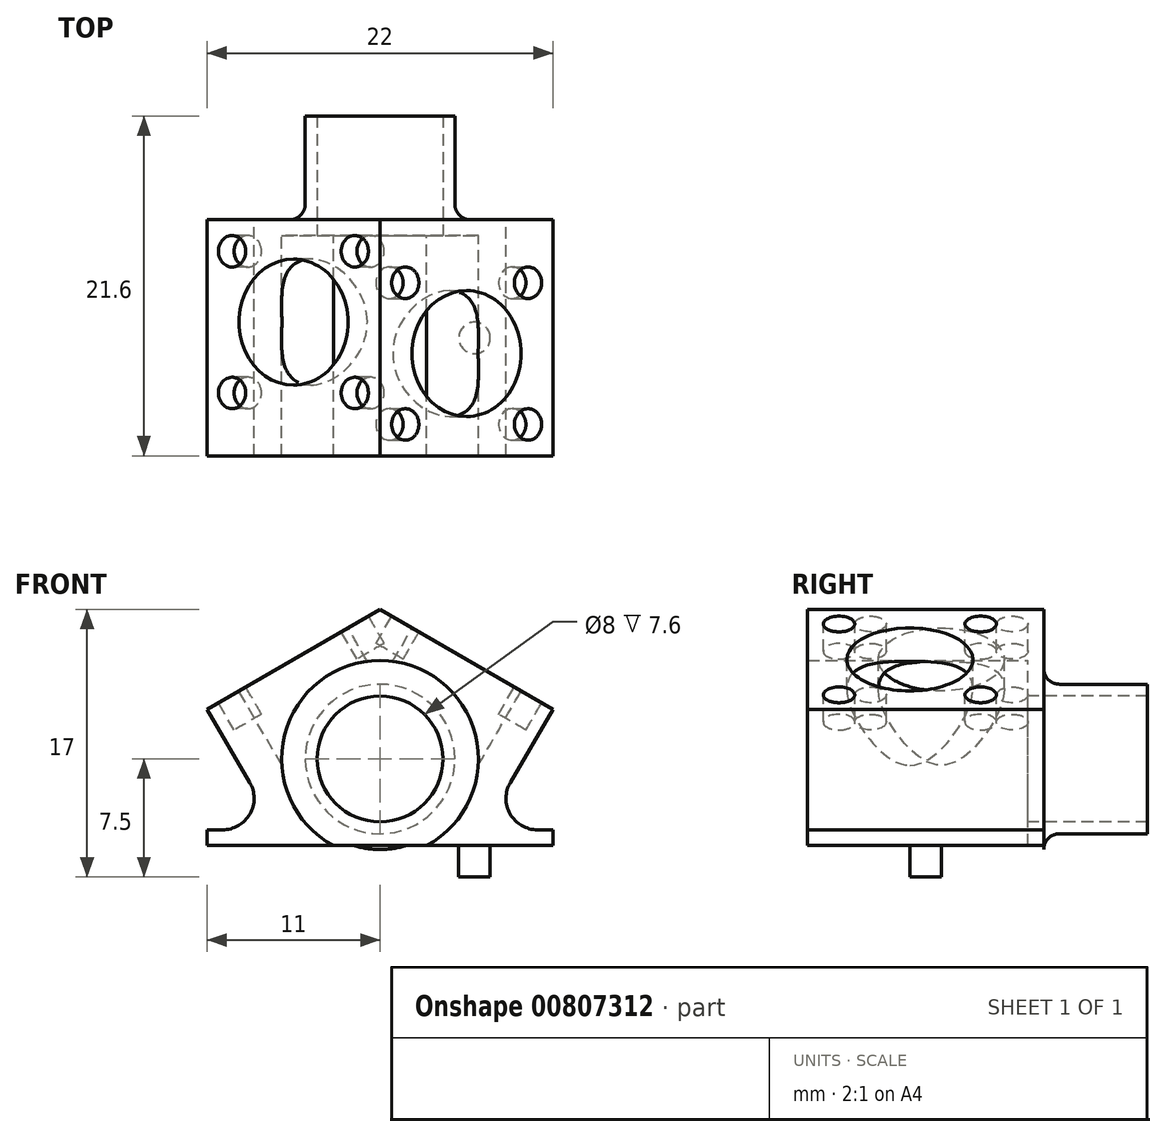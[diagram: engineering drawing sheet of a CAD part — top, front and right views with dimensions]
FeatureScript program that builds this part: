
annotation { "Feature Type Name" : "Feature", "Feature Type Description" : "" }
export const myFeature = defineFeature(function(context is Context, id is Id, definition is map)
    precondition{}
    {
        {
            var Q0;
            Q0=qCreatedBy(makeId("Front.planeOp"),FACE);
            var sketch = newSketch(context, id + "F0", { "sketchPlane" : qUnion([Q0])});
            skCircle(sketch, "E0", {"center": v(0, 0) * mm, "radius": 4 * mm});
            skCircle(sketch, "E1", {"center": v(0, 0) * mm, "radius": 6.25 * mm});
            skLineSegment(sketch, "E2", {"start": v(0, 9.5) * mm, "end": v(0, -7.5) * mm, "construction": true});
            skLineSegment(sketch, "E3", {"start": v(-11, 0) * mm, "end": v(11, 0) * mm, "construction": true});
            skLineSegment(sketch, "E4", {"start": v(-11, -7.5) * mm, "end": v(11, -7.5) * mm});
            skPoint(sketch, "E5", {"position": v(0, -7.5) * mm});
            skLineSegment(sketch, "E6", {"start": v(-11, -7.5) * mm, "end": v(-11, 9.5) * mm});
            skLineSegment(sketch, "E7.MirrorCS", {"start": v(11, -7.5) * mm, "end": v(11, 9.5) * mm});
            skLineSegment(sketch, "E8", {"start": v(-11, 9.5) * mm, "end": v(11, 9.5) * mm});
            skLineSegment(sketch, "E9", {"start": v(0, 9.5) * mm, "end": v(-11, 3.15) * mm});
            skLineSegment(sketch, "E10.MirrorCS", {"start": v(0, 9.5) * mm, "end": v(11, 3.15) * mm});
            skPoint(sketch, "E11", {"position": v(-11, -4.5) * mm});
            skArc(sketch, "E12", {"start": v(-11, -0.77) * mm, "mid": v(-12, -2.5) * mm, "end": v(-11, -4.23) * mm, "construction": true});
            skArc(sketch, "E13", {"start": v(-11, -4.23) * mm, "mid": v(-10.52, -4.43) * mm, "end": v(-10, -4.5) * mm, "construction": true});
            skLineSegment(sketch, "E14", {"start": v(-11, 3.15) * mm, "end": v(-8.28, -1.49) * mm});
            skArc(sketch, "E15", {"start": v(-8.28, -1.49) * mm, "mid": v(-9.49, -0.57) * mm, "end": v(-11, -0.77) * mm, "construction": true});
            skLineSegment(sketch, "E16", {"start": v(-11, -4.5) * mm, "end": v(-10, -4.5) * mm});
            skArc(sketch, "E17", {"start": v(-10, -4.5) * mm, "mid": v(-8.26, -3.5) * mm, "end": v(-8.28, -1.49) * mm});
            skLineSegment(sketch, "E18.MirrorCS", {"start": v(11, 3.15) * mm, "end": v(8.28, -1.49) * mm});
            skArc(sketch, "E19.MirrorCS", {"start": v(10, -4.5) * mm, "mid": v(8.26, -3.5) * mm, "end": v(8.28, -1.49) * mm});
            skLineSegment(sketch, "E20.MirrorCS", {"start": v(11, -4.5) * mm, "end": v(10, -4.5) * mm});
            skCircle(sketch, "E21", {"center": v(0, 0) * mm, "radius": 4.75 * mm});
            skSolve(sketch);
        }
        {
            var Q0;
            Q0=makeQuery(id+"F0.imprint","IMPRINT",FACE,{"disambiguationData":[TD([[makeQuery(id+"F0.imprint","IMPRINT",EDGE,{"derivedFrom":sQuery(id+"F0.wireOp",EDGE,"E1")}),-1.0]])]});
            extrude(context, id + "F1", {"entities" : qUnion([Q0]), "depth" : 13 * mm, "offsetDistance" : 25 * mm});
        }
        {
            var Q0;
            Q0=makeQuery(id+"F0.imprint","IMPRINT",FACE,{"disambiguationData":[TD([[makeQuery(id+"F0.imprint","IMPRINT",EDGE,{"derivedFrom":sQuery(id+"F0.wireOp",EDGE,"E1")}),1.0]])]});
            var Q1;
            Q1=makeQuery(id+"F0.imprint","IMPRINT",FACE,{"disambiguationData":[TD([[makeQuery(id+"F0.imprint","IMPRINT",EDGE,{"derivedFrom":sQuery(id+"F0.wireOp",EDGE,"E0")}),-1.0]])]});
            var Q2;
            Q2=makeQuery(id+"F0.imprint","IMPRINT",FACE,{"disambiguationData":[TD([[makeQuery(id+"F0.imprint","IMPRINT",EDGE,{"derivedFrom":sQuery(id+"F0.wireOp",EDGE,"E1")}),-1.0]])]});
            extrude(context, id + "F2", {"entities" : qUnion([Q0, Q1, Q2]), "operationType" : NewBodyOperationType.ADD, "oppositeDirection" : true, "depth" : 2 * mm, "offsetDistance" : 25 * mm});
        }
        {
            var Q0;
            Q0=makeQuery(id+"F0.imprint","IMPRINT",FACE,{"disambiguationData":[TD([[makeQuery(id+"F0.imprint","IMPRINT",EDGE,{"derivedFrom":sQuery(id+"F0.wireOp",EDGE,"E0")}),-1.0]])]});
            extrude(context, id + "F3", {"entities" : qUnion([Q0]), "operationType" : NewBodyOperationType.ADD, "oppositeDirection" : true, "depth" : 8.6 * mm, "offsetDistance" : 25 * mm});
        }
        {
            var Q0;
            Q0=makeQuery(id+"F3.boolean.opBoolean","INTERSECT",EDGE,{"derivedFrom":[makeQuery(id+"F2.opExtrude","CAP_FACE",FACE,{"disambiguationData":[OSD([sQuery(id+"F0.wireOp",EDGE,"E0"),sQuery(id+"F0.wireOp",EDGE,"E4"),sQuery(id+"F0.wireOp",EDGE,"E6"),sQuery(id+"F0.wireOp",EDGE,"E7.MirrorCS"),sQuery(id+"F0.wireOp",EDGE,"E9"),sQuery(id+"F0.wireOp",EDGE,"E10.MirrorCS"),sQuery(id+"F0.wireOp",EDGE,"E14"),sQuery(id+"F0.wireOp",EDGE,"E16"),sQuery(id+"F0.wireOp",EDGE,"E17"),sQuery(id+"F0.wireOp",EDGE,"E18.MirrorCS"),sQuery(id+"F0.wireOp",EDGE,"E19.MirrorCS"),sQuery(id+"F0.wireOp",EDGE,"E20.MirrorCS")])],"isStart":false}),makeQuery(id+"F3.opExtrude","SWEPT_FACE",FACE,{"disambiguationData":[OSD([sQuery(id+"F0.wireOp",EDGE,"E21")])]})]});
            fillet(context, id + "F4", {"entities" : qUnion([Q0]), "radius" : 1 * mm, "tangentPropagation" : true, "allowEdgeOverflow" : false});
        }
        {
            var Q0;
            {var subQ0=sQuery(id+"F0.wireOp",EDGE,"E10.MirrorCS");Q0=makeQuery(id+"F2.boolean.opBoolean","MERGE",FACE,{"derivedFrom":[makeQuery(id+"F1.opExtrude","SWEPT_FACE",FACE,{"disambiguationData":[OSD([subQ0])]}),makeQuery(id+"F2.opExtrude","SWEPT_FACE",FACE,{"disambiguationData":[OSD([subQ0])]})]});}
            var sketch = newSketch(context, id + "F5", { "sketchPlane" : qUnion([Q0])});
            skLineSegment(sketch, "E22.0", {"start": v(-4.75, -13) * mm, "end": v(7.95, -13) * mm});
            skLineSegment(sketch, "E23.0", {"start": v(-4.75, -13) * mm, "end": v(-4.75, 2) * mm});
            skLineSegment(sketch, "E24.0", {"start": v(-4.75, 2) * mm, "end": v(7.95, 2) * mm});
            skLineSegment(sketch, "E25.0", {"start": v(7.95, -13) * mm, "end": v(7.95, 2) * mm});
            skCircle(sketch, "E26", {"center": v(1.6, -6.5) * mm, "radius": 4 * mm});
            skLineSegment(sketch, "E27.bottom", {"start": v(-2.9, -2) * mm, "end": v(6.1, -2) * mm, "construction": true});
            skLineSegment(sketch, "E27.top", {"start": v(-2.9, -11) * mm, "end": v(6.1, -11) * mm, "construction": true});
            skLineSegment(sketch, "E27.left", {"start": v(-2.9, -2) * mm, "end": v(-2.9, -11) * mm, "construction": true});
            skLineSegment(sketch, "E27.right", {"start": v(6.1, -2) * mm, "end": v(6.1, -11) * mm, "construction": true});
            skCircle(sketch, "E28", {"center": v(-2.9, -11) * mm, "radius": 1 * mm});
            skCircle(sketch, "E29", {"center": v(6.1, -11) * mm, "radius": 1 * mm});
            skCircle(sketch, "E30", {"center": v(6.1, -2) * mm, "radius": 1 * mm});
            skCircle(sketch, "E31", {"center": v(-2.9, -2) * mm, "radius": 1 * mm});
            skSolve(sketch);
        }
        {
            var Q0;
            {var subQ0=sQuery(id+"F0.wireOp",EDGE,"E9");Q0=makeQuery(id+"F2.boolean.opBoolean","MERGE",FACE,{"derivedFrom":[makeQuery(id+"F1.opExtrude","SWEPT_FACE",FACE,{"disambiguationData":[OSD([subQ0])]}),makeQuery(id+"F2.opExtrude","SWEPT_FACE",FACE,{"disambiguationData":[OSD([subQ0])]})]});}
            var sketch = newSketch(context, id + "F6", { "sketchPlane" : qUnion([Q0])});
            skLineSegment(sketch, "E32.0", {"start": v(4.75, 2) * mm, "end": v(-7.95, 2) * mm});
            skLineSegment(sketch, "E33.0", {"start": v(4.75, -13) * mm, "end": v(4.75, 2) * mm});
            skLineSegment(sketch, "E34.0", {"start": v(4.75, -13) * mm, "end": v(-7.95, -13) * mm});
            skLineSegment(sketch, "E35.0", {"start": v(-7.95, -13) * mm, "end": v(-7.95, 2) * mm});
            skCircle(sketch, "E36", {"center": v(-1.6, -4.5) * mm, "radius": 4 * mm});
            skLineSegment(sketch, "E37.bottom", {"start": v(-6.1, 0) * mm, "end": v(2.9, 0) * mm, "construction": true});
            skLineSegment(sketch, "E37.top", {"start": v(-6.1, -9) * mm, "end": v(2.9, -9) * mm, "construction": true});
            skLineSegment(sketch, "E37.left", {"start": v(-6.1, 0) * mm, "end": v(-6.1, -9) * mm, "construction": true});
            skLineSegment(sketch, "E37.right", {"start": v(2.9, 0) * mm, "end": v(2.9, -9) * mm, "construction": true});
            skCircle(sketch, "E38", {"center": v(-6.1, -9) * mm, "radius": 1 * mm});
            skCircle(sketch, "E39", {"center": v(2.9, -9) * mm, "radius": 1 * mm});
            skCircle(sketch, "E40", {"center": v(2.9, 0) * mm, "radius": 1 * mm});
            skCircle(sketch, "E41", {"center": v(-6.1, 0) * mm, "radius": 1 * mm});
            skSolve(sketch);
        }
        {
            var Q0;
            Q0=makeQuery(id+"F5.imprint","IMPRINT",FACE,{"disambiguationData":[TD([[makeQuery(id+"F5.imprint","IMPRINT",EDGE,{"derivedFrom":sQuery(id+"F5.wireOp",EDGE,"E26")}),1.0]])]});
            var Q1;
            Q1=makeQuery(id+"F1.opExtrude","SWEPT_FACE",FACE,{"disambiguationData":[OSD([sQuery(id+"F0.wireOp",EDGE,"E1")])]});
            extrude(context, id + "F7", {"entities" : qUnion([Q0]), "operationType" : NewBodyOperationType.REMOVE, "endBound" : BoundingType.UP_TO_SURFACE, "oppositeDirection" : true, "depth" : 25 * mm, "endBoundEntityFace" : qUnion([Q1]), "offsetDistance" : 25 * mm});
        }
        {
            var Q0;
            Q0=makeQuery(id+"F5.imprint","IMPRINT",FACE,{"disambiguationData":[TD([[makeQuery(id+"F5.imprint","IMPRINT",EDGE,{"derivedFrom":sQuery(id+"F5.wireOp",EDGE,"E31")}),1.0]])]});
            var Q1;
            Q1=makeQuery(id+"F5.imprint","IMPRINT",FACE,{"disambiguationData":[TD([[makeQuery(id+"F5.imprint","IMPRINT",EDGE,{"derivedFrom":sQuery(id+"F5.wireOp",EDGE,"E30")}),1.0]])]});
            var Q2;
            Q2=makeQuery(id+"F5.imprint","IMPRINT",FACE,{"disambiguationData":[TD([[makeQuery(id+"F5.imprint","IMPRINT",EDGE,{"derivedFrom":sQuery(id+"F5.wireOp",EDGE,"E29")}),1.0]])]});
            var Q3;
            Q3=makeQuery(id+"F5.imprint","IMPRINT",FACE,{"disambiguationData":[TD([[makeQuery(id+"F5.imprint","IMPRINT",EDGE,{"derivedFrom":sQuery(id+"F5.wireOp",EDGE,"E28")}),1.0]])]});
            extrude(context, id + "F8", {"entities" : qUnion([Q0, Q1, Q2, Q3]), "operationType" : NewBodyOperationType.REMOVE, "oppositeDirection" : true, "depth" : 2 * mm, "offsetDistance" : 25 * mm});
        }
        {
            var Q0;
            Q0=makeQuery(id+"F6.imprint","IMPRINT",FACE,{"disambiguationData":[TD([[makeQuery(id+"F6.imprint","IMPRINT",EDGE,{"derivedFrom":sQuery(id+"F6.wireOp",EDGE,"E36")}),1.0]])]});
            var Q1;
            Q1=makeQuery(id+"F1.opExtrude","SWEPT_FACE",FACE,{"disambiguationData":[OSD([sQuery(id+"F0.wireOp",EDGE,"E1")])]});
            extrude(context, id + "F9", {"entities" : qUnion([Q0]), "operationType" : NewBodyOperationType.REMOVE, "endBound" : BoundingType.UP_TO_SURFACE, "oppositeDirection" : true, "depth" : 25 * mm, "endBoundEntityFace" : qUnion([Q1]), "offsetDistance" : 25 * mm});
        }
        {
            var Q0;
            Q0=makeQuery(id+"F6.imprint","IMPRINT",FACE,{"disambiguationData":[TD([[makeQuery(id+"F6.imprint","IMPRINT",EDGE,{"derivedFrom":sQuery(id+"F6.wireOp",EDGE,"E38")}),1.0]])]});
            var Q1;
            Q1=makeQuery(id+"F6.imprint","IMPRINT",FACE,{"disambiguationData":[TD([[makeQuery(id+"F6.imprint","IMPRINT",EDGE,{"derivedFrom":sQuery(id+"F6.wireOp",EDGE,"E41")}),1.0]])]});
            var Q2;
            Q2=makeQuery(id+"F6.imprint","IMPRINT",FACE,{"disambiguationData":[TD([[makeQuery(id+"F6.imprint","IMPRINT",EDGE,{"derivedFrom":sQuery(id+"F6.wireOp",EDGE,"E40")}),1.0]])]});
            var Q3;
            Q3=makeQuery(id+"F6.imprint","IMPRINT",FACE,{"disambiguationData":[TD([[makeQuery(id+"F6.imprint","IMPRINT",EDGE,{"derivedFrom":sQuery(id+"F6.wireOp",EDGE,"E39")}),1.0]])]});
            extrude(context, id + "F10", {"entities" : qUnion([Q0, Q1, Q2, Q3]), "operationType" : NewBodyOperationType.REMOVE, "oppositeDirection" : true, "depth" : 2 * mm, "offsetDistance" : 25 * mm});
        }
        {
            var Q0;
            Q0=makeQuery(id+"F0.imprint","IMPRINT",FACE,{"disambiguationData":[TD([[makeQuery(id+"F0.imprint","IMPRINT",EDGE,{"derivedFrom":sQuery(id+"F0.wireOp",EDGE,"E1")}),1.0]])]});
            var Q1;
            Q1=makeQuery(id+"F0.imprint","IMPRINT",FACE,{"disambiguationData":[TD([[makeQuery(id+"F0.imprint","IMPRINT",EDGE,{"derivedFrom":sQuery(id+"F0.wireOp",EDGE,"E0")}),-1.0]])]});
            extrude(context, id + "F11", {"entities" : qUnion([Q0, Q1]), "operationType" : NewBodyOperationType.REMOVE, "oppositeDirection" : true, "depth" : 1 * mm, "offsetDistance" : 25 * mm});
        }
        {
            var Q0;
            {var subQ0=sQuery(id+"F0.wireOp",EDGE,"E4");Q0=makeQuery(id+"F2.boolean.opBoolean","MERGE",FACE,{"derivedFrom":[makeQuery(id+"F1.opExtrude","SWEPT_FACE",FACE,{"disambiguationData":[OSD([subQ0])]}),makeQuery(id+"F2.opExtrude","SWEPT_FACE",FACE,{"disambiguationData":[OSD([subQ0])]})]});}
            var sketch = newSketch(context, id + "F12", { "sketchPlane" : qUnion([Q0])});
            skLineSegment(sketch, "E42.0", {"start": v(-11, 13) * mm, "end": v(-11, -2) * mm});
            skLineSegment(sketch, "E43.0", {"start": v(-11, 13) * mm, "end": v(11, 13) * mm});
            skLineSegment(sketch, "E44.0", {"start": v(11, 13) * mm, "end": v(11, -2) * mm});
            skLineSegment(sketch, "E45.0", {"start": v(-11, -2) * mm, "end": v(11, -2) * mm});
            skCircle(sketch, "E46", {"center": v(-6, 5.5) * mm, "radius": 1 * mm});
            skLineSegment(sketch, "E47", {"start": v(0, 13) * mm, "end": v(0, -2) * mm, "construction": true});
            skCircle(sketch, "E48.MirrorC", {"center": v(6, 5.5) * mm, "radius": 1 * mm});
            skSolve(sketch);
        }
        {
            var Q0;
            Q0=makeQuery(id+"F12.imprint","IMPRINT",FACE,{"disambiguationData":[TD([[makeQuery(id+"F12.imprint","IMPRINT",EDGE,{"derivedFrom":sQuery(id+"F12.wireOp",EDGE,"E46")}),1.0]])]});
            var Q1;
            Q1=makeQuery(id+"F12.imprint","IMPRINT",FACE,{"disambiguationData":[TD([[makeQuery(id+"F12.imprint","IMPRINT",EDGE,{"derivedFrom":sQuery(id+"F12.wireOp",EDGE,"E48.MirrorC")}),-1.0]])]});
            extrude(context, id + "F13", {"entities" : qUnion([Q0, Q1]), "operationType" : NewBodyOperationType.REMOVE, "oppositeDirection" : true, "depth" : 2 * mm, "offsetDistance" : 25 * mm});
        }
    });
